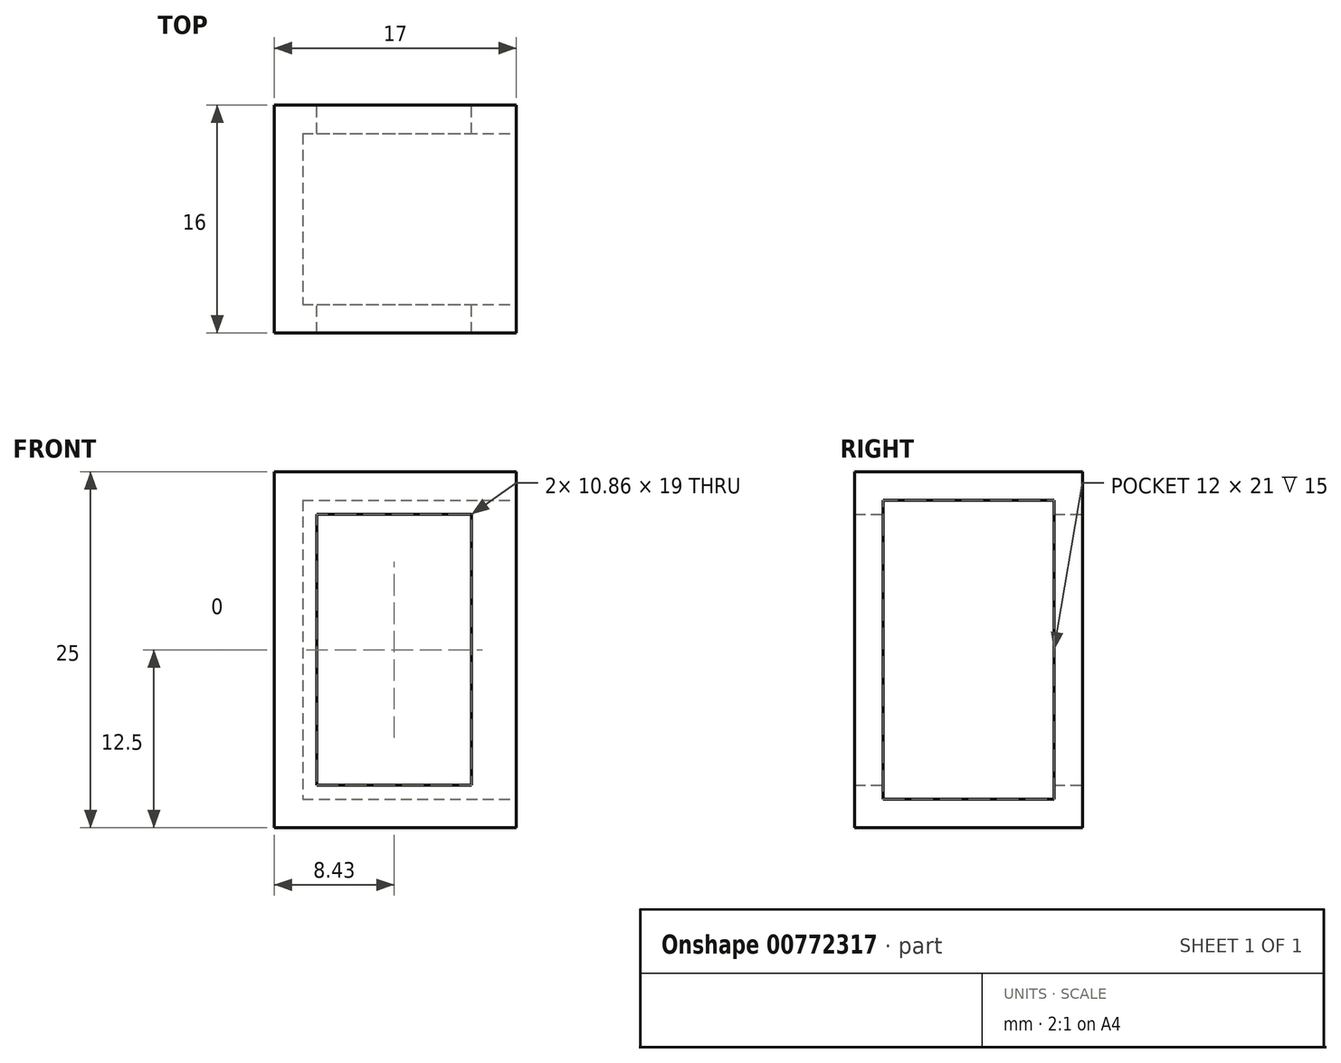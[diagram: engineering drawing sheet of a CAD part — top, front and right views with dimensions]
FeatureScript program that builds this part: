
annotation { "Feature Type Name" : "Feature", "Feature Type Description" : "" }
export const myFeature = defineFeature(function(context is Context, id is Id, definition is map)
    precondition{}
    {
        {
            var Q0;
            Q0=qCreatedBy(makeId("Front.planeOp"),FACE);
            var sketch = newSketch(context, id + "F0", { "sketchPlane" : qUnion([Q0])});
            skLineSegment(sketch, "E0.bottom", {"start": v(0, 25) * mm, "end": v(17, 25) * mm});
            skLineSegment(sketch, "E0.top", {"start": v(0, 0) * mm, "end": v(17, 0) * mm});
            skLineSegment(sketch, "E0.left", {"start": v(0, 25) * mm, "end": v(0, 0) * mm});
            skLineSegment(sketch, "E0.right", {"start": v(17, 25) * mm, "end": v(17, 0) * mm});
            skSolve(sketch);
        }
        {
            var Q0;
            Q0 = qSketchRegion(id + "F0", true);
            extrude(context, id + "F1", {"entities" : qUnion([Q0]), "oppositeDirection" : true, "depth" : 16 * mm, "offsetDistance" : 25 * mm});
        }
        {
            var Q0;
            Q0=makeQuery(id+"F1.opExtrude","SWEPT_FACE",FACE,{"disambiguationData":[OSD([sQuery(id+"F0.wireOp",EDGE,"E0.right")])]});
            shell(context, id + "F2", {"entities" : qUnion([Q0]), "thickness" : 2 * mm});
        }
        {
            var Q0;
            Q0=makeQuery(id+"F1.opExtrude","CAP_FACE",FACE,{"disambiguationData":[OSD([sQuery(id+"F0.wireOp",EDGE,"E0.bottom"),sQuery(id+"F0.wireOp",EDGE,"E0.top"),sQuery(id+"F0.wireOp",EDGE,"E0.left"),sQuery(id+"F0.wireOp",EDGE,"E0.right")])],"isStart":false});
            var sketch = newSketch(context, id + "F3", { "sketchPlane" : qUnion([Q0])});
            skLineSegment(sketch, "E1.bottom", {"start": v(-13.86, 22) * mm, "end": v(-3, 22) * mm});
            skLineSegment(sketch, "E1.top", {"start": v(-13.86, 3) * mm, "end": v(-3, 3) * mm});
            skLineSegment(sketch, "E1.left", {"start": v(-13.86, 22) * mm, "end": v(-13.86, 3) * mm});
            skLineSegment(sketch, "E1.right", {"start": v(-3, 22) * mm, "end": v(-3, 3) * mm});
            skSolve(sketch);
        }
        {
            var Q0;
            Q0 = qSketchRegion(id + "F3", true);
            extrude(context, id + "F4", {"entities" : qUnion([Q0]), "operationType" : NewBodyOperationType.REMOVE, "endBound" : BoundingType.THROUGH_ALL, "oppositeDirection" : true, "depth" : 5.6 * mm, "offsetDistance" : 25 * mm});
        }
    });
